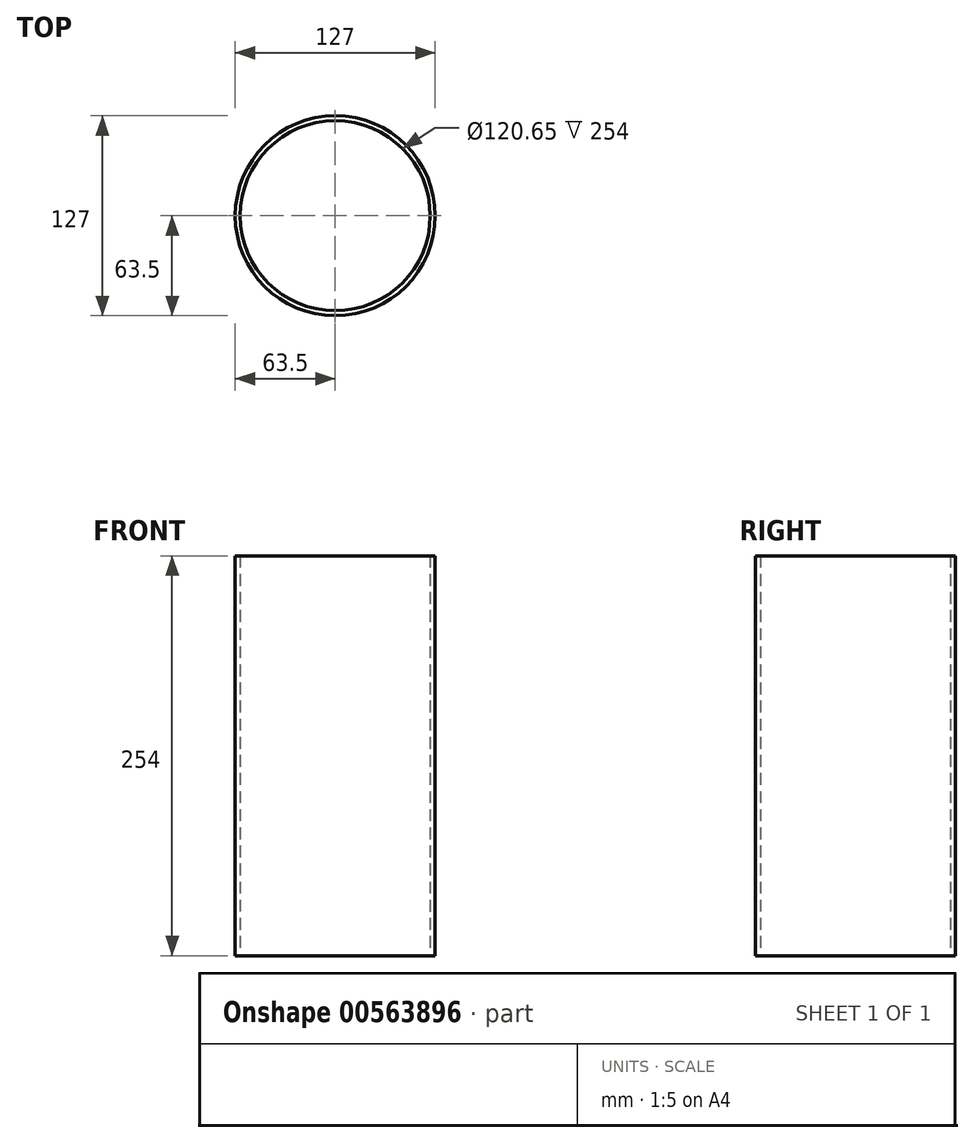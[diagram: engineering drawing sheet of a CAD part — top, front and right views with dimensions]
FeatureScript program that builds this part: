
annotation { "Feature Type Name" : "Feature", "Feature Type Description" : "" }
export const myFeature = defineFeature(function(context is Context, id is Id, definition is map)
    precondition{}
    {
        {
            var Q0;
            Q0=qCreatedBy(makeId("Top.planeOp"),FACE);
            var sketch = newSketch(context, id + "F0", { "sketchPlane" : qUnion([Q0])});
            skCircle(sketch, "E0", {"center": v(0, 0) * mm, "radius": 63.5 * mm});
            skCircle(sketch, "E1", {"center": v(0, 0) * mm, "radius": 60.33 * mm});
            skSolve(sketch);
        }
        {
            var Q0;
            Q0 = qSketchRegion(id + "F0", true);
            extrude(context, id + "F1", {"entities" : qUnion([Q0]), "depth" : 254 * mm, "offsetDistance" : 25.4 * mm});
        }
    });
